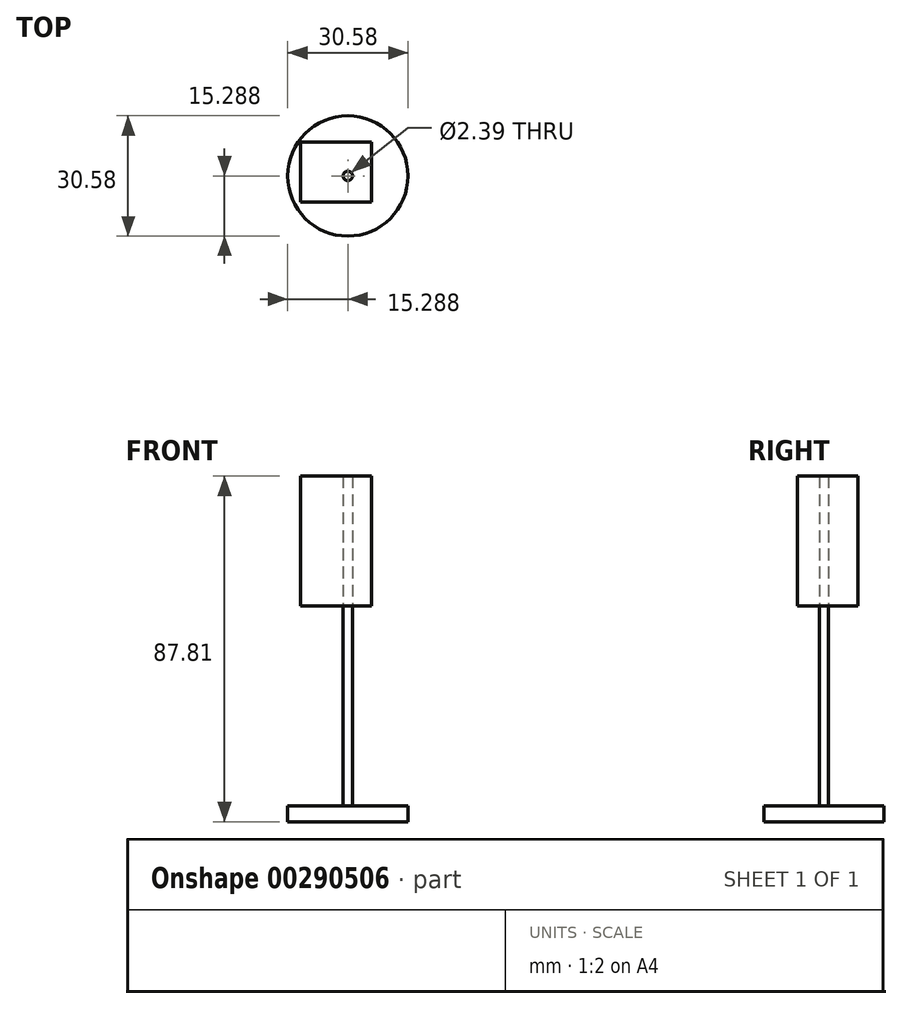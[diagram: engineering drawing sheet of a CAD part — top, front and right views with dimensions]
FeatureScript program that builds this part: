
annotation { "Feature Type Name" : "Feature", "Feature Type Description" : "" }
export const myFeature = defineFeature(function(context is Context, id is Id, definition is map)
    precondition{}
    {
        {
            var Q0;
            Q0=qCreatedBy(makeId("Top.planeOp"),FACE);
            var sketch = newSketch(context, id + "F0", { "sketchPlane" : qUnion([Q0])});
            skCircle(sketch, "E0", {"center": v(58.03, 62.12) * mm, "radius": 15.3 * mm});
            skSolve(sketch);
        }
        {
            var Q0;
            Q0=makeQuery(id+"F0.imprint","IMPRINT",FACE,{"disambiguationData":[TD([[makeQuery(id+"F0.imprint","IMPRINT",EDGE,{"derivedFrom":sQuery(id+"F0.wireOp",EDGE,"E0")}),1.0]])]});
            extrude(context, id + "F1", {"entities" : qUnion([Q0]), "depth" : 4.1 * mm});
        }
        {
            var Q0;
            Q0=makeQuery(id+"F1.opExtrude","CAP_FACE",FACE,{"disambiguationData":[OSD([sQuery(id+"F0.wireOp",EDGE,"E0")])],"isStart":false});
            var sketch = newSketch(context, id + "F2", { "sketchPlane" : qUnion([Q0])});
            skCircle(sketch, "E1", {"center": v(58.03, 62.12) * mm, "radius": 1.2 * mm});
            skSolve(sketch);
        }
        {
            var Q0;
            Q0 = qSketchRegion(id + "F2", true);
            extrude(context, id + "F3", {"entities" : qUnion([Q0]), "operationType" : NewBodyOperationType.ADD, "depth" : 50.76 * mm});
        }
        {
            var Q0;
            Q0=makeQuery(id+"F3.opExtrude","CAP_FACE",FACE,{"disambiguationData":[OSD([sQuery(id+"F2.wireOp",EDGE,"E1")])],"isStart":false});
            var sketch = newSketch(context, id + "F4", { "sketchPlane" : qUnion([Q0])});
            skLineSegment(sketch, "E2.bottom", {"start": v(46.02, 70.76) * mm, "end": v(64.01, 70.76) * mm});
            skLineSegment(sketch, "E2.top", {"start": v(46.02, 55.43) * mm, "end": v(64.01, 55.43) * mm});
            skLineSegment(sketch, "E2.left", {"start": v(46.02, 70.76) * mm, "end": v(46.02, 55.43) * mm});
            skLineSegment(sketch, "E2.right", {"start": v(64.01, 70.76) * mm, "end": v(64.01, 55.43) * mm});
            skSolve(sketch);
        }
        {
            var Q0;
            Q0=makeQuery(id+"F4.imprint","IMPRINT",FACE,{"disambiguationData":[TD([[makeQuery(id+"F4.imprint","IMPRINT",EDGE,{"derivedFrom":sQuery(id+"F4.wireOp",EDGE,"E2.bottom")}),-1.0]])]});
            extrude(context, id + "F5", {"entities" : qUnion([Q0]), "depth" : 32.95 * mm});
        }
    });
